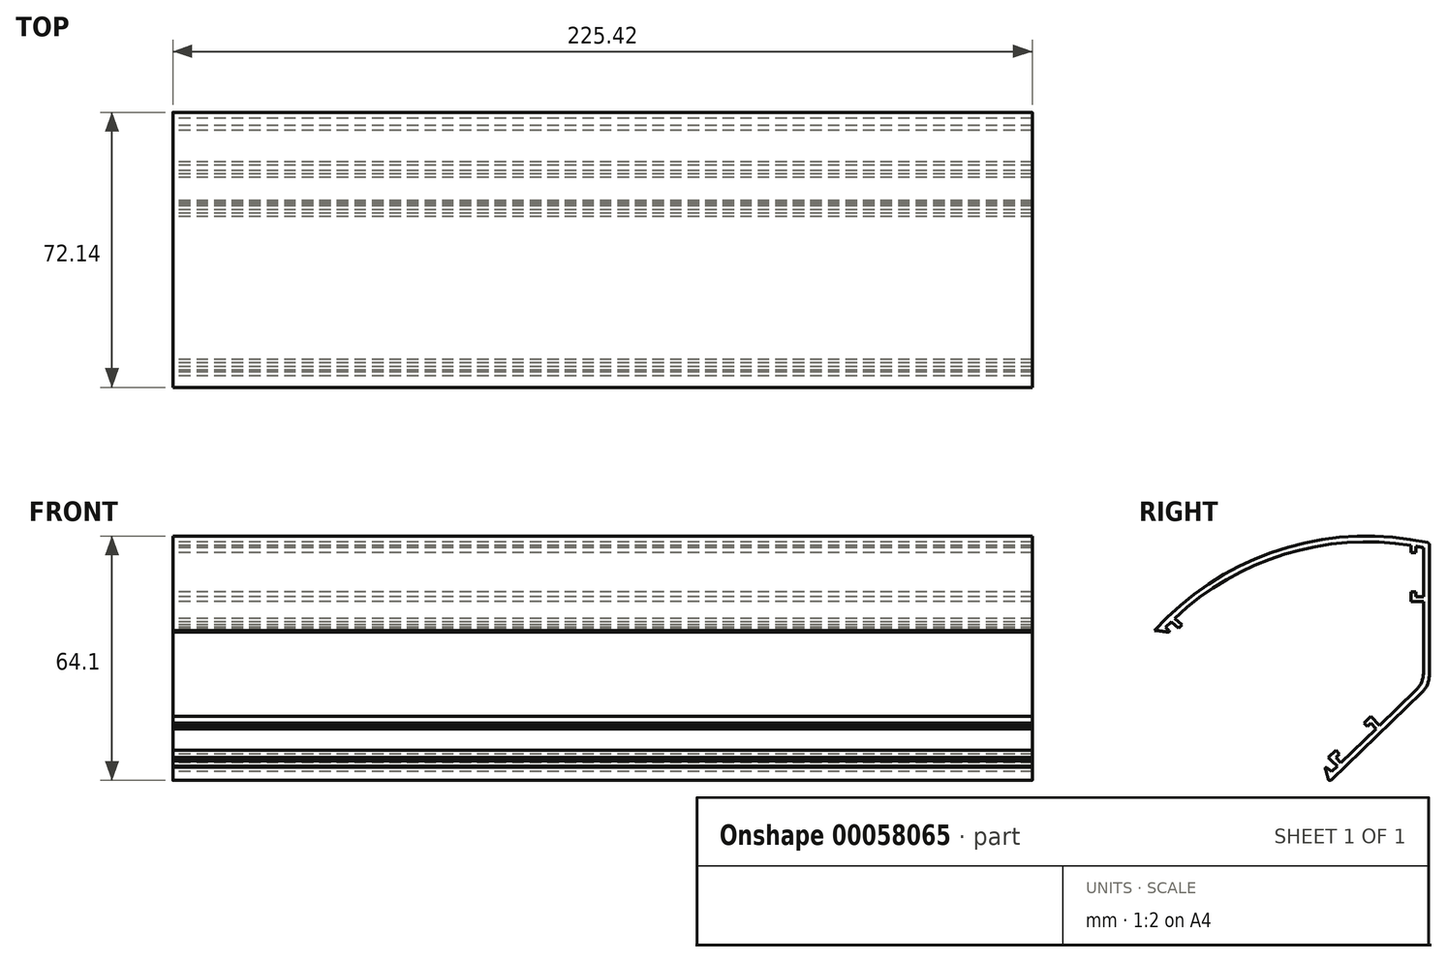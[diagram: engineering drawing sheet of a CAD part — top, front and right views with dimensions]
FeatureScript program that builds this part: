
annotation { "Feature Type Name" : "Feature", "Feature Type Description" : "" }
export const myFeature = defineFeature(function(context is Context, id is Id, definition is map)
    precondition{}
    {
        {
            var Q0;
            Q0=qCreatedBy(makeId("Right.planeOp"),FACE);
            var sketch = newSketch(context, id + "F0", { "sketchPlane" : qUnion([Q0])});
            skLineSegment(sketch, "E0", {"start": v(-26.31, -25.4) * mm, "end": v(0, 0) * mm});
            skLineSegment(sketch, "E1", {"start": v(0, 0) * mm, "end": v(0, 37.34) * mm});
            skArc(sketch, "E2", {"start": v(0, 37.34) * mm, "mid": v(-36.86, 36.32) * mm, "end": v(-68.74, 17.77) * mm});
            skLineSegment(sketch, "E3", {"start": v(-68.74, 17.77) * mm, "end": v(-72.14, 14.43) * mm});
            skLineSegment(sketch, "E4", {"start": v(-26.31, -25.4) * mm, "end": v(-72.14, 14.43) * mm});
            skLineSegment(sketch, "E5", {"start": v(-68.74, 17.77) * mm, "end": v(-26.31, -25.4) * mm, "construction": true});
            skSolve(sketch);
        }
        {
            var Q0;
            Q0 = qSketchRegion(id + "F0", true);
            extrude(context, id + "F1", {"entities" : qUnion([Q0]), "endBound" : BoundingType.SYMMETRIC, "depth" : 225.42 * mm});
        }
        {
            var Q0;
            Q0=makeQuery(id+"F1.opExtrude","SWEPT_FACE",FACE,{"disambiguationData":[OSD([sQuery(id+"F0.wireOp",EDGE,"E4")])]});
            var Q1;
            Q1=makeQuery(id+"F1.opExtrude","CAP_FACE",FACE,{"disambiguationData":[OSD([sQuery(id+"F0.wireOp",EDGE,"E0"),sQuery(id+"F0.wireOp",EDGE,"E1"),sQuery(id+"F0.wireOp",EDGE,"E2"),sQuery(id+"F0.wireOp",EDGE,"E3"),sQuery(id+"F0.wireOp",EDGE,"E4")])],"isStart":true});
            var Q2;
            Q2=makeQuery(id+"F1.opExtrude","CAP_FACE",FACE,{"disambiguationData":[OSD([sQuery(id+"F0.wireOp",EDGE,"E0"),sQuery(id+"F0.wireOp",EDGE,"E1"),sQuery(id+"F0.wireOp",EDGE,"E2"),sQuery(id+"F0.wireOp",EDGE,"E3"),sQuery(id+"F0.wireOp",EDGE,"E4")])],"isStart":false});
            shell(context, id + "F2", {"entities" : qUnion([Q0, Q1, Q2]), "thickness" : 1.52 * mm});
        }
        {
            var Q0;
            Q0=makeQuery(id+"F1.opExtrude","CAP_FACE",FACE,{"disambiguationData":[OSD([sQuery(id+"F0.wireOp",EDGE,"E0"),sQuery(id+"F0.wireOp",EDGE,"E1"),sQuery(id+"F0.wireOp",EDGE,"E2"),sQuery(id+"F0.wireOp",EDGE,"E3"),sQuery(id+"F0.wireOp",EDGE,"E4")])],"isStart":true});
            var sketch = newSketch(context, id + "F3", { "sketchPlane" : qUnion([Q0])});
            skLineSegment(sketch, "E6", {"start": v(72.14, 14.43) * mm, "end": v(26.31, -25.4) * mm, "construction": true});
            skSolve(sketch);
        }
        {
            var Q0;
            {var subQ6=sQuery(id+"F0.wireOp",EDGE,"E0");var subQ7=makeQuery(id+"F1.opExtrude","CAP_EDGE",EDGE,{"disambiguationData":[OSD([subQ6])],"isStart":true});Q0=makeQuery(id+"F3.imprint","IMPRINT",FACE,{"disambiguationData":[TD([[makeQuery(id+"F3.imprint","IMPRINT",EDGE,{"derivedFrom":subQ7}),-1.0]])]});}
            var sketch = newSketch(context, id + "F4", { "sketchPlane" : qUnion([Q0])});
            skLineSegment(sketch, "E7", {"start": v(70.98, 13.42) * mm, "end": v(69.17, 15.2) * mm});
            skLineSegment(sketch, "E8", {"start": v(69.17, 15.2) * mm, "end": v(67.25, 13.54) * mm});
            skLineSegment(sketch, "E9", {"start": v(67.25, 13.54) * mm, "end": v(69.07, 11.76) * mm});
            skLineSegment(sketch, "E10", {"start": v(69.07, 11.76) * mm, "end": v(70.98, 13.42) * mm});
            skSolve(sketch);
        }
        {
            var Q0;
            Q0 = qSketchRegion(id + "F4", true);
            var Q1;
            Q1=makeQuery(id+"F1.opExtrude","CAP_FACE",FACE,{"disambiguationData":[OSD([sQuery(id+"F0.wireOp",EDGE,"E0"),sQuery(id+"F0.wireOp",EDGE,"E1"),sQuery(id+"F0.wireOp",EDGE,"E2"),sQuery(id+"F0.wireOp",EDGE,"E3"),sQuery(id+"F0.wireOp",EDGE,"E4")])],"isStart":false});
            extrude(context, id + "F5", {"entities" : qUnion([Q0]), "operationType" : NewBodyOperationType.ADD, "endBound" : BoundingType.UP_TO_SURFACE, "oppositeDirection" : true, "endBoundEntityFace" : qUnion([Q1]), "depth" : 25.4 * mm});
        }
        {
            var Q0;
            {var subQ6=sQuery(id+"F0.wireOp",EDGE,"E0");var subQ7=makeQuery(id+"F1.opExtrude","CAP_EDGE",EDGE,{"disambiguationData":[OSD([subQ6])],"isStart":true});Q0=makeQuery(id+"F3.imprint","IMPRINT",FACE,{"disambiguationData":[TD([[makeQuery(id+"F3.imprint","IMPRINT",EDGE,{"derivedFrom":subQ7}),-1.0]])]});}
            var sketch = newSketch(context, id + "F6", { "sketchPlane" : qUnion([Q0])});
            skLineSegment(sketch, "E11", {"start": v(25.64, -22.64) * mm, "end": v(27.47, -24.4) * mm});
            skLineSegment(sketch, "E12", {"start": v(27.47, -24.4) * mm, "end": v(29.38, -22.74) * mm});
            skLineSegment(sketch, "E13", {"start": v(29.38, -22.74) * mm, "end": v(27.55, -20.97) * mm});
            skLineSegment(sketch, "E14", {"start": v(27.55, -20.97) * mm, "end": v(25.64, -22.64) * mm});
            skSolve(sketch);
        }
        {
            var Q0;
            Q0 = qSketchRegion(id + "F6", true);
            var Q1;
            Q1=makeQuery(id+"F5.boolean.opBoolean","MERGE",FACE,{"derivedFrom":[makeQuery(id+"F1.opExtrude","CAP_FACE",FACE,{"disambiguationData":[OSD([sQuery(id+"F0.wireOp",EDGE,"E0"),sQuery(id+"F0.wireOp",EDGE,"E1"),sQuery(id+"F0.wireOp",EDGE,"E2"),sQuery(id+"F0.wireOp",EDGE,"E3"),sQuery(id+"F0.wireOp",EDGE,"E4")])],"isStart":false}),makeQuery(id+"F5.opExtrude","CAP_FACE",FACE,{"disambiguationData":[OSD([sQuery(id+"F4.wireOp",EDGE,"E7"),sQuery(id+"F4.wireOp",EDGE,"E8"),sQuery(id+"F4.wireOp",EDGE,"E9"),sQuery(id+"F4.wireOp",EDGE,"E10")])],"isStart":false})]});
            extrude(context, id + "F7", {"entities" : qUnion([Q0]), "operationType" : NewBodyOperationType.ADD, "endBound" : BoundingType.UP_TO_SURFACE, "oppositeDirection" : true, "endBoundEntityFace" : qUnion([Q1]), "depth" : 25.4 * mm});
        }
        {
            var Q0;
            {var subQ6=sQuery(id+"F0.wireOp",EDGE,"E0");var subQ7=makeQuery(id+"F1.opExtrude","CAP_EDGE",EDGE,{"disambiguationData":[OSD([subQ6])],"isStart":true});Q0=makeQuery(id+"F3.imprint","IMPRINT",FACE,{"disambiguationData":[TD([[makeQuery(id+"F3.imprint","IMPRINT",EDGE,{"derivedFrom":subQ7}),-1.0]])]});}
            var sketch = newSketch(context, id + "F8", { "sketchPlane" : qUnion([Q0])});
            skCircle(sketch, "E15", {"center": v(76.77, -37.18) * mm, "radius": 51.8 * mm});
            skSolve(sketch);
        }
        {
            var Q0;
            Q0 = qSketchRegion(id + "F8", true);
            var Q1;
            Q1=makeQuery(id+"F7.boolean.opBoolean","MERGE",FACE,{"derivedFrom":[makeQuery(id+"F5.boolean.opBoolean","MERGE",FACE,{"derivedFrom":[makeQuery(id+"F1.opExtrude","CAP_FACE",FACE,{"disambiguationData":[OSD([sQuery(id+"F0.wireOp",EDGE,"E0"),sQuery(id+"F0.wireOp",EDGE,"E1"),sQuery(id+"F0.wireOp",EDGE,"E2"),sQuery(id+"F0.wireOp",EDGE,"E3"),sQuery(id+"F0.wireOp",EDGE,"E4")])],"isStart":false}),makeQuery(id+"F5.opExtrude","CAP_FACE",FACE,{"disambiguationData":[OSD([sQuery(id+"F4.wireOp",EDGE,"E7"),sQuery(id+"F4.wireOp",EDGE,"E8"),sQuery(id+"F4.wireOp",EDGE,"E9"),sQuery(id+"F4.wireOp",EDGE,"E10")])],"isStart":false})]}),makeQuery(id+"F7.opExtrude","CAP_FACE",FACE,{"disambiguationData":[OSD([sQuery(id+"F6.wireOp",EDGE,"E11"),sQuery(id+"F6.wireOp",EDGE,"E12"),sQuery(id+"F6.wireOp",EDGE,"E13"),sQuery(id+"F6.wireOp",EDGE,"E14")])],"isStart":false})]});
            extrude(context, id + "F9", {"entities" : qUnion([Q0]), "operationType" : NewBodyOperationType.REMOVE, "endBound" : BoundingType.UP_TO_SURFACE, "oppositeDirection" : true, "endBoundEntityFace" : qUnion([Q1]), "depth" : 25.4 * mm});
        }
        {
            var Q0;
            {var subQ6=sQuery(id+"F0.wireOp",EDGE,"E0");var subQ7=makeQuery(id+"F1.opExtrude","CAP_EDGE",EDGE,{"disambiguationData":[OSD([subQ6])],"isStart":true});Q0=makeQuery(id+"F3.imprint","IMPRINT",FACE,{"disambiguationData":[TD([[makeQuery(id+"F3.imprint","IMPRINT",EDGE,{"derivedFrom":subQ7}),-1.0]])]});}
            var sketch = newSketch(context, id + "F10", { "sketchPlane" : qUnion([Q0])});
            skLineSegment(sketch, "E16", {"start": v(24.08, -21.14) * mm, "end": v(25.57, -19.85) * mm});
            skLineSegment(sketch, "E17", {"start": v(25.57, -19.85) * mm, "end": v(24.53, -18.85) * mm});
            skLineSegment(sketch, "E18", {"start": v(24.53, -18.85) * mm, "end": v(23.17, -20.26) * mm});
            skLineSegment(sketch, "E19", {"start": v(23.17, -20.26) * mm, "end": v(24.08, -21.14) * mm});
            skSolve(sketch);
        }
        {
            var Q0;
            {var subQ6=sQuery(id+"F0.wireOp",EDGE,"E0");var subQ7=makeQuery(id+"F1.opExtrude","CAP_EDGE",EDGE,{"disambiguationData":[OSD([subQ6])],"isStart":true});Q0=makeQuery(id+"F3.imprint","IMPRINT",FACE,{"disambiguationData":[TD([[makeQuery(id+"F3.imprint","IMPRINT",EDGE,{"derivedFrom":subQ7}),-1.0]])]});}
            var sketch = newSketch(context, id + "F11", { "sketchPlane" : qUnion([Q0])});
            skLineSegment(sketch, "E20", {"start": v(25.57, -19.85) * mm, "end": v(23.62, -17.97) * mm});
            skLineSegment(sketch, "E21", {"start": v(23.62, -17.97) * mm, "end": v(24.5, -17.06) * mm});
            skLineSegment(sketch, "E22", {"start": v(24.5, -17.06) * mm, "end": v(26.45, -18.94) * mm});
            skLineSegment(sketch, "E23", {"start": v(26.45, -18.94) * mm, "end": v(25.57, -19.85) * mm});
            skSolve(sketch);
        }
        {
            var Q0;
            {var subQ6=sQuery(id+"F0.wireOp",EDGE,"E0");var subQ7=makeQuery(id+"F1.opExtrude","CAP_EDGE",EDGE,{"disambiguationData":[OSD([subQ6])],"isStart":true});Q0=makeQuery(id+"F3.imprint","IMPRINT",FACE,{"disambiguationData":[TD([[makeQuery(id+"F3.imprint","IMPRINT",EDGE,{"derivedFrom":subQ7}),-1.0]])]});}
            var sketch = newSketch(context, id + "F12", { "sketchPlane" : qUnion([Q0])});
            skLineSegment(sketch, "E24", {"start": v(67.63, 16.72) * mm, "end": v(65.71, 15.05) * mm});
            skLineSegment(sketch, "E25", {"start": v(65.71, 15.05) * mm, "end": v(64.8, 15.94) * mm});
            skLineSegment(sketch, "E26", {"start": v(64.8, 15.94) * mm, "end": v(66.72, 17.6) * mm});
            skLineSegment(sketch, "E27", {"start": v(66.72, 17.6) * mm, "end": v(67.63, 16.72) * mm});
            skSolve(sketch);
        }
        {
            var Q0;
            {var subQ6=sQuery(id+"F0.wireOp",EDGE,"E0");var subQ7=makeQuery(id+"F1.opExtrude","CAP_EDGE",EDGE,{"disambiguationData":[OSD([subQ6])],"isStart":true});Q0=makeQuery(id+"F3.imprint","IMPRINT",FACE,{"disambiguationData":[TD([[makeQuery(id+"F3.imprint","IMPRINT",EDGE,{"derivedFrom":subQ7}),-1.0]])]});}
            var sketch = newSketch(context, id + "F13", { "sketchPlane" : qUnion([Q0])});
            skLineSegment(sketch, "E28", {"start": v(13.94, -11.35) * mm, "end": v(15.3, -9.94) * mm});
            skLineSegment(sketch, "E29", {"start": v(15.3, -9.94) * mm, "end": v(16.22, -10.82) * mm});
            skLineSegment(sketch, "E30", {"start": v(16.22, -10.82) * mm, "end": v(17.1, -9.9) * mm});
            skLineSegment(sketch, "E31", {"start": v(17.1, -9.9) * mm, "end": v(15.27, -8.14) * mm});
            skLineSegment(sketch, "E32", {"start": v(15.27, -8.14) * mm, "end": v(13.03, -10.47) * mm});
            skLineSegment(sketch, "E33", {"start": v(13.03, -10.47) * mm, "end": v(13.94, -11.35) * mm});
            skSolve(sketch);
        }
        {
            var Q0;
            {var subQ6=sQuery(id+"F12.wireOp",EDGE,"E27");Q0=makeQuery(id+"F12.imprint","IMPRINT",FACE,{"disambiguationData":[TD([[makeQuery(id+"F12.imprint","IMPRINT",EDGE,{"derivedFrom":subQ6}),1.0]])]});}
            var sketch = newSketch(context, id + "F14", { "sketchPlane" : qUnion([Q0])});
            skLineSegment(sketch, "E34", {"start": v(1.52, 22.01) * mm, "end": v(1.52, 23.28) * mm});
            skLineSegment(sketch, "E35", {"start": v(1.52, 23.28) * mm, "end": v(3.48, 23.28) * mm});
            skLineSegment(sketch, "E36", {"start": v(3.48, 23.28) * mm, "end": v(3.48, 24.55) * mm});
            skLineSegment(sketch, "E37", {"start": v(3.48, 24.55) * mm, "end": v(4.75, 24.55) * mm});
            skLineSegment(sketch, "E38", {"start": v(4.75, 24.55) * mm, "end": v(4.75, 22.01) * mm});
            skLineSegment(sketch, "E39", {"start": v(4.75, 22.01) * mm, "end": v(1.52, 22.01) * mm});
            skLineSegment(sketch, "E40", {"start": v(3.48, 36.7) * mm, "end": v(3.48, 34.84) * mm});
            skLineSegment(sketch, "E41", {"start": v(3.48, 34.84) * mm, "end": v(4.75, 34.84) * mm});
            skLineSegment(sketch, "E42", {"start": v(4.75, 34.84) * mm, "end": v(4.75, 36.7) * mm});
            skLineSegment(sketch, "E43", {"start": v(4.75, 36.7) * mm, "end": v(3.48, 36.7) * mm});
            skSolve(sketch);
        }
        {
            var Q0;
            Q0 = qSketchRegion(id + "F10", true);
            var Q1;
            Q1 = qSketchRegion(id + "F11", true);
            var Q2;
            Q2 = qSketchRegion(id + "F12", true);
            var Q3;
            Q3 = qSketchRegion(id + "F13", true);
            var Q4;
            Q4 = qSketchRegion(id + "F14", true);
            var Q5;
            Q5=makeQuery(id+"F7.boolean.opBoolean","MERGE",FACE,{"derivedFrom":[makeQuery(id+"F5.boolean.opBoolean","MERGE",FACE,{"derivedFrom":[makeQuery(id+"F1.opExtrude","CAP_FACE",FACE,{"disambiguationData":[OSD([sQuery(id+"F0.wireOp",EDGE,"E0"),sQuery(id+"F0.wireOp",EDGE,"E1"),sQuery(id+"F0.wireOp",EDGE,"E2"),sQuery(id+"F0.wireOp",EDGE,"E3"),sQuery(id+"F0.wireOp",EDGE,"E4")])],"isStart":false}),makeQuery(id+"F5.opExtrude","CAP_FACE",FACE,{"disambiguationData":[OSD([sQuery(id+"F4.wireOp",EDGE,"E7"),sQuery(id+"F4.wireOp",EDGE,"E8"),sQuery(id+"F4.wireOp",EDGE,"E9"),sQuery(id+"F4.wireOp",EDGE,"E10")])],"isStart":false})]}),makeQuery(id+"F7.opExtrude","CAP_FACE",FACE,{"disambiguationData":[OSD([sQuery(id+"F6.wireOp",EDGE,"E11"),sQuery(id+"F6.wireOp",EDGE,"E12"),sQuery(id+"F6.wireOp",EDGE,"E13"),sQuery(id+"F6.wireOp",EDGE,"E14")])],"isStart":false})]});
            extrude(context, id + "F15", {"entities" : qUnion([Q0, Q1, Q2, Q3, Q4]), "operationType" : NewBodyOperationType.ADD, "endBound" : BoundingType.UP_TO_SURFACE, "oppositeDirection" : true, "endBoundEntityFace" : qUnion([Q5]), "depth" : 25.4 * mm});
        }
        {
            var Q0;
            Q0=makeQuery(id+"F1.opExtrude","SWEPT_EDGE",EDGE,{"disambiguationData":[OSD([sQuery(id+"F0.wireOp",EDGE,"E0"),sQuery(id+"F0.wireOp",EDGE,"E4")])]});
            var Q1;
            Q1=makeQuery(id+"F1.opExtrude","SWEPT_EDGE",EDGE,{"disambiguationData":[OSD([sQuery(id+"F0.wireOp",EDGE,"E3"),sQuery(id+"F0.wireOp",EDGE,"E4")])]});
            var Q2;
            Q2=makeQuery(id+"F1.opExtrude","SWEPT_EDGE",EDGE,{"disambiguationData":[OSD([sQuery(id+"F0.wireOp",EDGE,"E1"),sQuery(id+"F0.wireOp",EDGE,"E2")])]});
            fillet(context, id + "F16", {"entities" : qUnion([Q0, Q1, Q2]), "radius" : 0.5 * mm, "allowEdgeOverflow" : false});
        }
        {
            var Q0;
            Q0=makeQuery(id+"F2.opShell","OFFSET_EDGE",EDGE,{"disambiguationData":[OSD([sQuery(id+"F0.wireOp",EDGE,"E0"),sQuery(id+"F0.wireOp",EDGE,"E1")])]});
            var Q1;
            Q1=makeQuery(id+"F1.opExtrude","SWEPT_EDGE",EDGE,{"disambiguationData":[OSD([sQuery(id+"F0.wireOp",EDGE,"E0"),sQuery(id+"F0.wireOp",EDGE,"E1")])]});
            fillet(context, id + "F17", {"entities" : qUnion([Q0, Q1]), "radius" : 6.35 * mm, "tangentPropagation" : true, "allowEdgeOverflow" : false});
        }
        {
            var Q0;
            Q0=makeQuery(id+"F7.opExtrude","SWEPT_EDGE",EDGE,{"disambiguationData":[OSD([sQuery(id+"F6.wireOp",EDGE,"E13"),sQuery(id+"F6.wireOp",EDGE,"E14")])]});
            var Q1;
            Q1=makeQuery(id+"F9.boolean.opBoolean","INTERSECT",EDGE,{"derivedFrom":[makeQuery(id+"F5.opExtrude","SWEPT_FACE",FACE,{"disambiguationData":[OSD([sQuery(id+"F4.wireOp",EDGE,"E8")])]}),makeQuery(id+"F9.opExtrude","SWEPT_FACE",FACE,{"disambiguationData":[OSD([sQuery(id+"F8.wireOp",EDGE,"E15")])]})]});
            fillet(context, id + "F18", {"entities" : qUnion([Q0, Q1]), "radius" : 0.25 * mm, "tangentPropagation" : true, "allowEdgeOverflow" : false});
        }
    });
